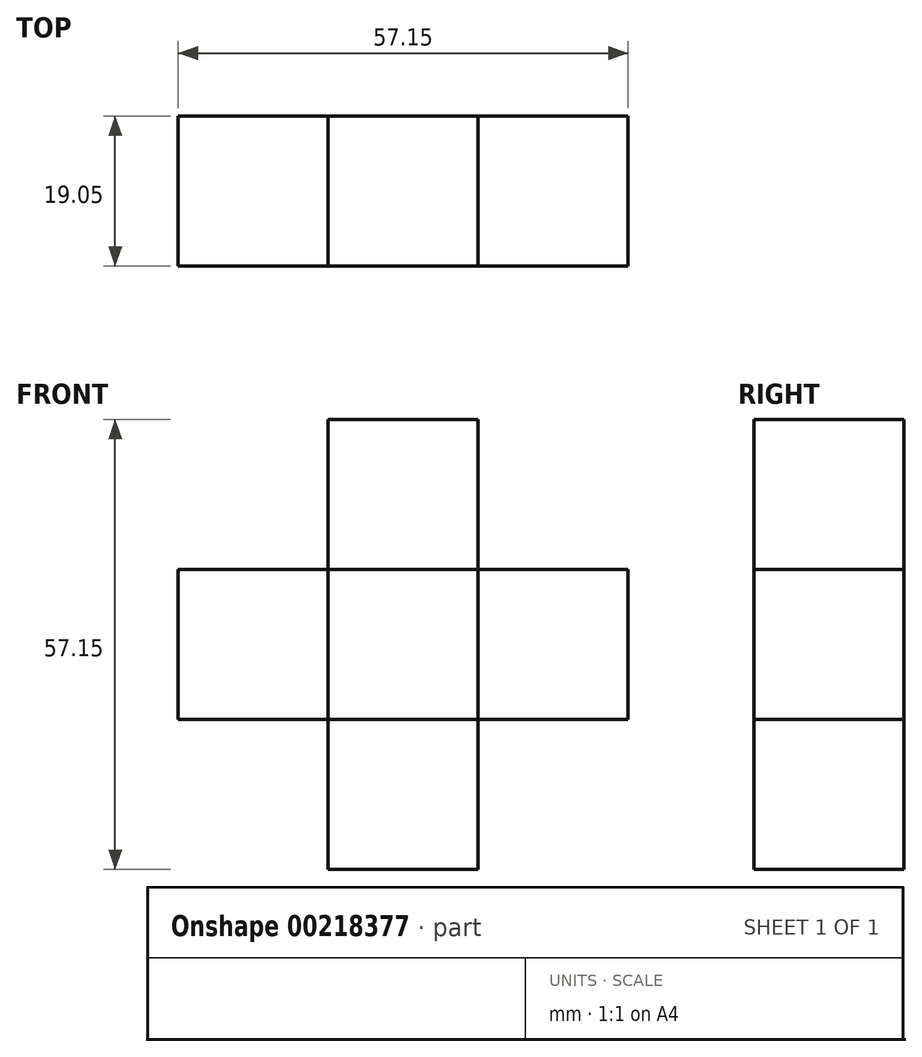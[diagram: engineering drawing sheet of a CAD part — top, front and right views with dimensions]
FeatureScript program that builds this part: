
annotation { "Feature Type Name" : "Feature", "Feature Type Description" : "" }
export const myFeature = defineFeature(function(context is Context, id is Id, definition is map)
    precondition{}
    {
        {
            var Q0;
            Q0=qCreatedBy(makeId("Front.planeOp"),FACE);
            var sketch = newSketch(context, id + "F0", { "sketchPlane" : qUnion([Q0])});
            skLineSegment(sketch, "E0.bottom", {"start": v(-4.42, 38.1) * mm, "end": v(14.63, 38.1) * mm});
            skLineSegment(sketch, "E0.top", {"start": v(-4.42, 19.05) * mm, "end": v(14.63, 19.05) * mm});
            skLineSegment(sketch, "E0.left", {"start": v(-4.42, 38.1) * mm, "end": v(-4.42, 19.05) * mm});
            skLineSegment(sketch, "E0.right", {"start": v(14.63, 38.1) * mm, "end": v(14.63, 19.05) * mm});
            skLineSegment(sketch, "E1.bottom", {"start": v(-23.47, 38.1) * mm, "end": v(-4.42, 38.1) * mm});
            skLineSegment(sketch, "E1.top", {"start": v(-23.47, 19.05) * mm, "end": v(-4.42, 19.05) * mm});
            skLineSegment(sketch, "E1.left", {"start": v(-23.47, 38.1) * mm, "end": v(-23.47, 19.05) * mm});
            skLineSegment(sketch, "E2.bottom", {"start": v(14.63, 38.1) * mm, "end": v(33.68, 38.1) * mm});
            skLineSegment(sketch, "E2.top", {"start": v(14.63, 19.05) * mm, "end": v(33.68, 19.05) * mm});
            skLineSegment(sketch, "E2.right", {"start": v(33.68, 38.1) * mm, "end": v(33.68, 19.05) * mm});
            skLineSegment(sketch, "E3.bottom", {"start": v(-4.42, 0) * mm, "end": v(14.63, 0) * mm});
            skLineSegment(sketch, "E3.left", {"start": v(-4.42, 0) * mm, "end": v(-4.42, 19.05) * mm});
            skLineSegment(sketch, "E3.right", {"start": v(14.63, 0) * mm, "end": v(14.63, 19.05) * mm});
            skLineSegment(sketch, "E4.bottom", {"start": v(-4.42, 57.15) * mm, "end": v(14.63, 57.15) * mm});
            skLineSegment(sketch, "E4.left", {"start": v(-4.42, 57.15) * mm, "end": v(-4.42, 38.1) * mm});
            skLineSegment(sketch, "E4.right", {"start": v(14.63, 57.15) * mm, "end": v(14.63, 38.1) * mm});
            skLineSegment(sketch, "E5.bottom", {"start": v(-57.3, -16.61) * mm, "end": v(-38.25, -16.61) * mm});
            skLineSegment(sketch, "E5.top", {"start": v(-57.3, -35.66) * mm, "end": v(-38.25, -35.66) * mm});
            skLineSegment(sketch, "E5.left", {"start": v(-57.3, -16.61) * mm, "end": v(-57.3, -35.66) * mm});
            skLineSegment(sketch, "E5.right", {"start": v(-38.25, -16.61) * mm, "end": v(-38.25, -35.66) * mm});
            skLineSegment(sketch, "E6.bottom", {"start": v(-57.3, -54.71) * mm, "end": v(-38.25, -54.71) * mm});
            skLineSegment(sketch, "E6.left", {"start": v(-57.3, -54.71) * mm, "end": v(-57.3, -35.66) * mm});
            skLineSegment(sketch, "E6.right", {"start": v(-38.25, -54.71) * mm, "end": v(-38.25, -35.66) * mm});
            skSolve(sketch);
        }
        {
            var Q0;
            Q0=makeQuery(id+"F0.imprint","IMPRINT",FACE,{"disambiguationData":[TD([[makeQuery(id+"F0.imprint","IMPRINT",EDGE,{"derivedFrom":sQuery(id+"F0.wireOp",EDGE,"E4.bottom")}),-1.0]])]});
            var Q1;
            Q1=makeQuery(id+"F0.imprint","IMPRINT",FACE,{"disambiguationData":[TD([[makeQuery(id+"F0.imprint","IMPRINT",EDGE,{"derivedFrom":sQuery(id+"F0.wireOp",EDGE,"E1.bottom")}),-1.0]])]});
            var Q2;
            Q2=makeQuery(id+"F0.imprint","IMPRINT",FACE,{"disambiguationData":[TD([[makeQuery(id+"F0.imprint","IMPRINT",EDGE,{"derivedFrom":sQuery(id+"F0.wireOp",EDGE,"E0.left")}),1.0]])]});
            var Q3;
            Q3=makeQuery(id+"F0.imprint","IMPRINT",FACE,{"disambiguationData":[TD([[makeQuery(id+"F0.imprint","IMPRINT",EDGE,{"derivedFrom":sQuery(id+"F0.wireOp",EDGE,"E2.bottom")}),-1.0]])]});
            var Q4;
            Q4=makeQuery(id+"F0.imprint","IMPRINT",FACE,{"disambiguationData":[TD([[makeQuery(id+"F0.imprint","IMPRINT",EDGE,{"derivedFrom":sQuery(id+"F0.wireOp",EDGE,"E3.bottom")}),1.0]])]});
            extrude(context, id + "F1", {"entities" : qUnion([Q0, Q1, Q2, Q3, Q4]), "depth" : 19.05 * mm});
        }
    });
